# Revit family: Cisterns-ToiletCisterns-Vitra-İntegraSeries_5428L003-0107
name_source: partatom
category: Plumbing Fixtures
revit_build: Autodesk Revit 2017 (Build: 20160225_1515(x64)
units: mm (PartAtom-declared; Revit-internal decimal feet)

## family parameters
Cut with Voids When Loaded = No
Host = Face
OmniClass Number = 23.45.05.21.11
OmniClass Title = Water Closets
Part Type = Normal
Room Calculation Point = No
Round Connector Dimension = Use Diameter
Shared = Yes

## types (2) — shared parameters
BIMobject category = Toilet Cisterns
CW Connection = Yes
Color = White
Default Elevation = 410 mm  [stored 1.34514 ft]
Design country = Turkey
HW Connection = No
IFC Classification = Sanitary Terminal
Main Material = Ceramic
Manufacturer = Vitra
Manufacturer name = Vitra
MountingType = WC Face Mounted
NBS Referans Code = 35-93-90
NBS Referans Description = Wc Cisterns
Nominal Depth (mm) = 140 mm
Nominal Height (mm) = 410 mm  [stored 1.34514 ft]
Nominal Width (mm) = 385 mm  [stored 1.26312 ft]
OmniClass Code = 23-31 19 19
OmniClass Description = Water Closets
Product certification = https://vitraglobal.com
Product data url = https://www.vitra.com.tr
Product group = WC Cisterns
Secondary Material = Ceramic-White
Technical description = https://www.vitra.com.tr
URL = https://www.vitra.com.tr
Uniclass 2.0 Code = PR-35-93-90
Uniclass 2.0 Description = Wc Cisterns
Uniclass 2015 Code = Pr_40_20_93_89
Uniclass 2015 Name = WC cisterns
Vent Connection = No
Warranty Period (Year) = 10 Years
Waste Connection = No
Weight Net (kg) = 14,925
Youtube = https://www.youtube.com
zero-valued in all types: Cost

## per-type parameters (varying)
| type | Article No. (default) | Description | Model | Product SKU | Product family |
| Cistern_ToiletCisterns-Vitra_5428L003-0107 | 5428L003-0107 | VitrA İntegra WC Cisterns | 5428L003-0107 | 5428L003-0107 | İntegra |
| Cistern_ToiletCisterns-Vitra_5428B003-5560 | 5428B003-5560 | VitrA WC Cisterns | 5428B003-5560 | 5428B003-5560 | Universal |

note: [stored X ft] marks values corroborated as IEEE doubles in the binary element streams (Revit-internal decimal feet)

## geometry (parser evidence)
native form markers: Sweep x2
no freeform markers — native parametric forms only
